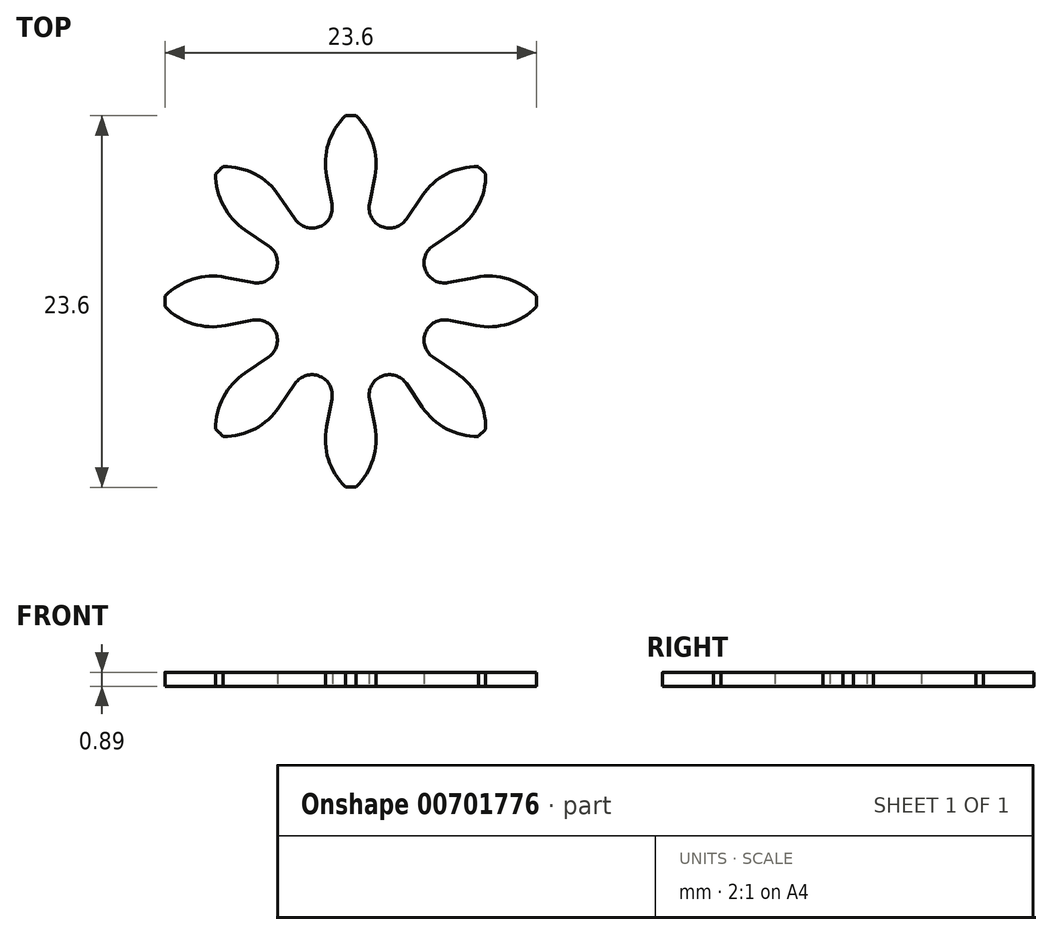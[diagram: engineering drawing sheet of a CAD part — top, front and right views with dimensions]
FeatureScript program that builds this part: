
annotation { "Feature Type Name" : "Feature", "Feature Type Description" : "" }
export const myFeature = defineFeature(function(context is Context, id is Id, definition is map)
    precondition{}
    {
        {
            var Q0;
            Q0=qCreatedBy(makeId("Top.planeOp"),FACE);
            var sketch = newSketch(context, id + "F0", { "sketchPlane" : qUnion([Q0])});
            skCircle(sketch, "E0", {"center": v(0, 0) * mm, "radius": 5.14 * mm});
            skArc(sketch, "E1", {"start": v(-5.23, 7.5) * mm, "mid": v(3.5, -8.45) * mm, "end": v(-1.6, 9) * mm});
            skArc(sketch, "E2", {"start": v(-8.1, 8.57) * mm, "mid": v(4.51, -10.9) * mm, "end": v(-0.33, 11.8) * mm});
            skPoint(sketch, "E3.orphan", {"position": v(0, 14.68) * mm});
            skPoint(sketch, "E4.orphan", {"position": v(-1.61, 0) * mm});
            skPoint(sketch, "E5.end.orphan", {"position": v(1.61, 0) * mm});
            skArc(sketch, "E6.1.1", {"start": v(-8.1, 8.57) * mm, "mid": v(-6.08, 8.1) * mm, "end": v(-4.54, 6.7) * mm});
            skLineSegment(sketch, "E6.1.2", {"start": v(-3.53, 5.22) * mm, "end": v(-4.54, 6.7) * mm});
            skPoint(sketch, "E7.orphan", {"position": v(-4.77, 7.05) * mm});
            skArc(sketch, "E8.1.2", {"start": v(-0.33, 11.8) * mm, "mid": v(-1.42, 10.02) * mm, "end": v(-1.53, 7.95) * mm});
            skLineSegment(sketch, "E8.1.3", {"start": v(-1.2, 6.19) * mm, "end": v(-1.53, 7.95) * mm});
            skPoint(sketch, "E9.orphan", {"position": v(-1.61, 8.35) * mm});
            skArc(sketch, "E10", {"start": v(-3.53, 5.22) * mm, "mid": v(-1.97, 4.75) * mm, "end": v(-1.2, 6.19) * mm});
            skPoint(sketch, "E10.first.point", {"position": v(-1.2, 6.19) * mm});
            skPoint(sketch, "E10.second.point", {"position": v(-3.53, 5.22) * mm});
            skPoint(sketch, "E10.third.point", {"position": v(-1.97, 4.75) * mm});
            skPoint(sketch, "E11.orphan", {"position": v(0.33, 11.8) * mm});
            skPoint(sketch, "E12.orphan", {"position": v(-4.26, 2.88) * mm});
            skPoint(sketch, "E13.orphan", {"position": v(-8.57, 8.1) * mm});
            skPoint(sketch, "E14.orphan", {"position": v(-2.88, 4.26) * mm});
            skPoint(sketch, "E15.orphan", {"position": v(-0.97, 5.05) * mm});
            skSolve(sketch);
        }
        {
            var Q0;
            Q0 = qSketchRegion(id + "F0", true);
            extrude(context, id + "F1", {"entities" : qUnion([Q0]), "depth" : 0.89 * mm, "offsetDistance" : 25.4 * mm});
        }
        {
            var Q0;
            Q0=makeQuery(id+"F1.opExtrude","SWEPT_FACE",FACE,{"disambiguationData":[OSD([sQuery(id+"F0.wireOp",EDGE,"E8.1.2")])]});
            var Q1;
            Q1=makeQuery(id+"F1.opExtrude","SWEPT_FACE",FACE,{"disambiguationData":[OSD([sQuery(id+"F0.wireOp",EDGE,"E8.1.3")])]});
            var Q2;
            Q2=makeQuery(id+"F1.opExtrude","SWEPT_FACE",FACE,{"disambiguationData":[OSD([sQuery(id+"F0.wireOp",EDGE,"E10")])]});
            var Q3;
            Q3=makeQuery(id+"F1.opExtrude","SWEPT_FACE",FACE,{"disambiguationData":[OSD([sQuery(id+"F0.wireOp",EDGE,"E6.1.2")])]});
            var Q4;
            Q4=makeQuery(id+"F1.opExtrude","SWEPT_FACE",FACE,{"disambiguationData":[OSD([sQuery(id+"F0.wireOp",EDGE,"E6.1.1")])]});
            var Q5;
            Q5=makeQuery(id+"F1.opExtrude","SWEPT_FACE",FACE,{"disambiguationData":[OSD([sQuery(id+"F0.wireOp",EDGE,"E2")])]});
            circularPattern(context, id + "F2", {"patternType" : PatternType.FACE, "faces" : qUnion([Q0, Q1, Q2, Q3, Q4]), "axis" : qUnion([Q5]), "angle" : 360 * degree, "instanceCount" : 8, "equalSpace" : true});
        }
    });
